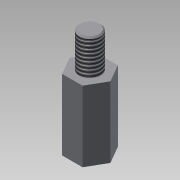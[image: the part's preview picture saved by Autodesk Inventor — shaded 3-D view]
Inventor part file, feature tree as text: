
AUTODESK INVENTOR PART (.ipt)
format: ipt  version: 2016 (Build 200138000, 138)  size: 125,952 bytes
history: native  units: mm
features: sketch x3, extrude x2, chamfer x2, hole x1, plane x1, mirror x1
ambient origin geometry x8: Origin, YZ Plane, XZ Plane, XY Plane, X Axis, Y Axis, Z Axis, Center Point
bodies: Solid1 (feature_tree)
feature tree (10):
  extrude  "Extrusion1"  Depth=10.0mm TaperAngle=0.0deg
  hole  "Hole1"  [1 undecoded]
  chamfer  "Chamfer2"  Distance=1.0mm
  extrude  "Extrusion3"  [1 undecoded]
  plane  "Work Plane1"
  mirror  "Mirror2"
  chamfer  "Chamfer3"  [1 undecoded]
  sketch  "Sketch1"  dims[d0=5.0mm d1=10.0mm d2=0.0mm]
  sketch  "Sketch3"  dims[d11=2.459mm d12=10.0mm d13=4.0mm d14=2.0mm d15=90.0deg d16=8.0mm d17=20.594885mm d18=0.5mm d19=2.0mm d20=45.0deg d21=1.0mm d22=-7.853982mm]
  sketch  "Sketch4"  dims[d23=0.5mm d24=2.0mm d25=45.0deg]
note: 3 required parameter values undecoded (feature->parameter linkage not recoverable at this tier; creation-order binding heuristic only, values carry confidence <= 0.55)
